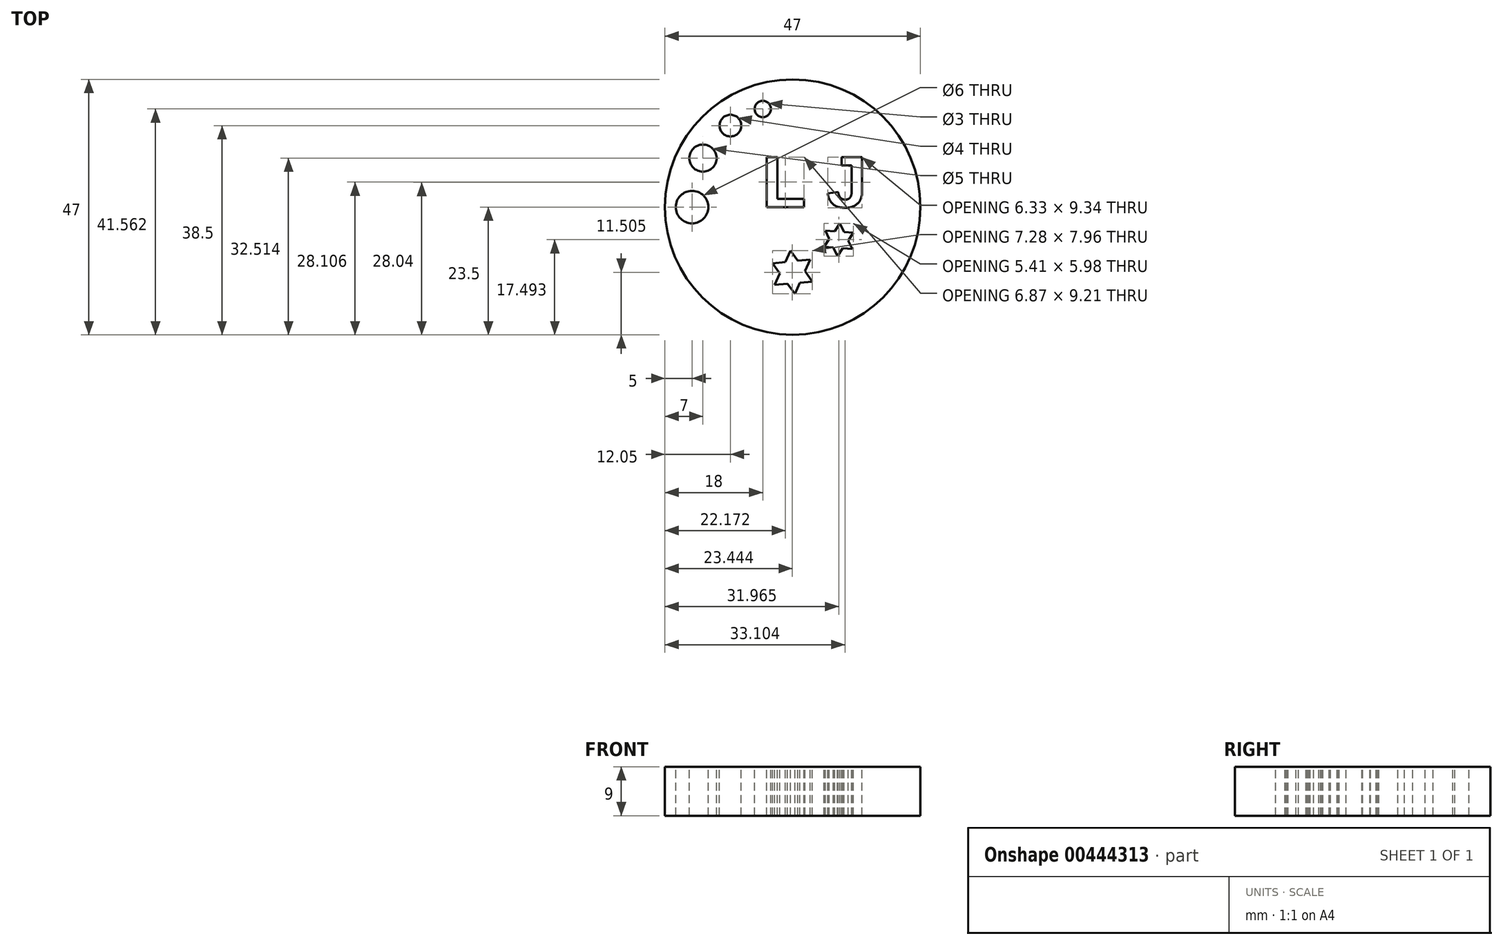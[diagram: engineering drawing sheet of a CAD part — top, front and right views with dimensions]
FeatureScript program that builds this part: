
annotation { "Feature Type Name" : "Feature", "Feature Type Description" : "" }
export const myFeature = defineFeature(function(context is Context, id is Id, definition is map)
    precondition{}
    {
        {
            var Q0;
            Q0=qCreatedBy(makeId("Top.planeOp"),FACE);
            var sketch = newSketch(context, id + "F0", { "sketchPlane" : qUnion([Q0])});
            skCircle(sketch, "E0", {"center": v(0, 0) * mm, "radius": 23.5 * mm});
            skSolve(sketch);
        }
        {
            var Q0;
            Q0=makeQuery(id+"F0.imprint","IMPRINT",FACE,{"disambiguationData":[TD([[makeQuery(id+"F0.imprint","IMPRINT",EDGE,{"derivedFrom":sQuery(id+"F0.wireOp",EDGE,"E0")}),1.0]])]});
            extrude(context, id + "F1", {"entities" : qUnion([Q0]), "depth" : 9 * mm});
        }
        {
            var Q0;
            Q0=makeQuery(id+"F1.opExtrude","CAP_FACE",FACE,{"disambiguationData":[OSD([sQuery(id+"F0.wireOp",EDGE,"E0")])],"isStart":false});
            var sketch = newSketch(context, id + "F2", { "sketchPlane" : qUnion([Q0])});
            skCircle(sketch, "E1", {"center": v(-18.5, 0) * mm, "radius": 3 * mm});
            skCircle(sketch, "E2", {"center": v(-16.5, 9.01) * mm, "radius": 2.5 * mm});
            skCircle(sketch, "E3", {"center": v(-11.45, 15) * mm, "radius": 2 * mm});
            skCircle(sketch, "E4", {"center": v(-5.5, 18.06) * mm, "radius": 1.5 * mm});
            skText(sketch, "E5", { "text": "L J", "fontName": "Arimo-Bold.ttf"});
            skCircle(sketch, "E6.cCircle", {"center": v(-0.04, -12) * mm, "radius": 4 * mm, "construction": true});
            skLineSegment(sketch, "E6.0", {"start": v(3.59, -13.7) * mm, "end": v(1.32, -13.9) * mm});
            skLineSegment(sketch, "E6.1", {"start": v(-3.32, -14.29) * mm, "end": v(-2.35, -12.23) * mm});
            skLineSegment(sketch, "E6.2", {"start": v(-0.38, -8.01) * mm, "end": v(0.92, -9.88) * mm});
            skLineSegment(sketch, "E7.0", {"start": v(3.19, -9.63) * mm, "end": v(2.25, -11.78) * mm});
            skLineSegment(sketch, "E7.1", {"start": v(0.4, -15.98) * mm, "end": v(-0.99, -14.09) * mm});
            skLineSegment(sketch, "E7.2", {"start": v(-3.7, -10.39) * mm, "end": v(-1.37, -10.13) * mm});
            skLineSegment(sketch, "E8.trimOffspring", {"start": v(0.92, -9.88) * mm, "end": v(3.19, -9.63) * mm});
            skLineSegment(sketch, "E9.trimOffspring", {"start": v(-1.37, -10.13) * mm, "end": v(-0.38, -8.01) * mm});
            skLineSegment(sketch, "E10.trimOffspring", {"start": v(-2.35, -12.23) * mm, "end": v(-3.7, -10.39) * mm});
            skLineSegment(sketch, "E11.trimOffspring", {"start": v(-0.99, -14.09) * mm, "end": v(-3.32, -14.29) * mm});
            skLineSegment(sketch, "E12.trimOffspring", {"start": v(1.32, -13.9) * mm, "end": v(0.4, -15.98) * mm});
            skLineSegment(sketch, "E13.trimOffspring", {"start": v(2.25, -11.78) * mm, "end": v(3.59, -13.7) * mm});
            skCircle(sketch, "E14.cCircle", {"center": v(8.47, -6) * mm, "radius": 3 * mm, "construction": true});
            skLineSegment(sketch, "E14.0", {"start": v(10.94, -7.7) * mm, "end": v(9.21, -7.57) * mm});
            skLineSegment(sketch, "E14.1", {"start": v(5.76, -7.3) * mm, "end": v(6.74, -5.87) * mm});
            skLineSegment(sketch, "E14.2", {"start": v(8.7, -3.02) * mm, "end": v(9.44, -4.58) * mm});
            skLineSegment(sketch, "E15.0", {"start": v(11.17, -4.71) * mm, "end": v(10.2, -6.14) * mm});
            skLineSegment(sketch, "E15.1", {"start": v(8.23, -9) * mm, "end": v(7.49, -7.44) * mm});
            skLineSegment(sketch, "E15.2", {"start": v(6, -4.31) * mm, "end": v(7.72, -4.44) * mm});
            skLineSegment(sketch, "E16.trimOffspring", {"start": v(9.44, -4.58) * mm, "end": v(11.17, -4.71) * mm});
            skLineSegment(sketch, "E17.trimOffspring", {"start": v(7.72, -4.44) * mm, "end": v(8.7, -3.02) * mm});
            skLineSegment(sketch, "E18.trimOffspring", {"start": v(6.74, -5.87) * mm, "end": v(6, -4.31) * mm});
            skLineSegment(sketch, "E19.trimOffspring", {"start": v(7.49, -7.44) * mm, "end": v(5.76, -7.3) * mm});
            skLineSegment(sketch, "E20.trimOffspring", {"start": v(9.21, -7.57) * mm, "end": v(8.23, -9) * mm});
            skLineSegment(sketch, "E21.trimOffspring", {"start": v(10.2, -6.14) * mm, "end": v(10.94, -7.7) * mm});
            skPoint(sketch, "E22", {"position": v(0, 0) * mm});
            const initialGuessF2  = {"E5": [-0.00566, 0, 1, 0, 0.00964]};
            skSetInitialGuess(sketch, initialGuessF2);
            skSolve(sketch);
        }
        {
            var Q0;
            Q0 = qSketchRegion(id + "F2", true);
            extrude(context, id + "F3", {"entities" : qUnion([Q0]), "operationType" : NewBodyOperationType.REMOVE, "endBound" : BoundingType.THROUGH_ALL, "oppositeDirection" : true, "depth" : 25 * mm});
        }
    });
